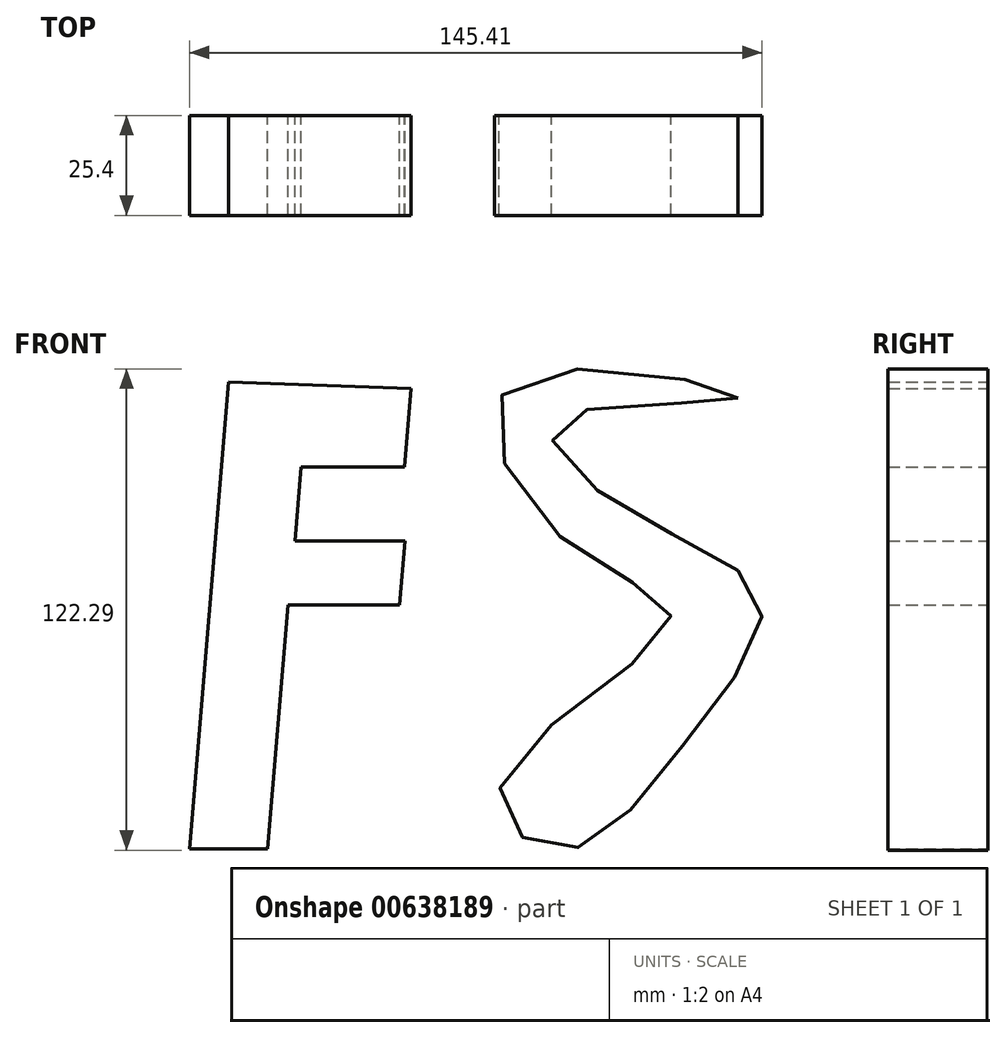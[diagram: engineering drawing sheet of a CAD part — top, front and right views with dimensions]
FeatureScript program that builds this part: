
annotation { "Feature Type Name" : "Feature", "Feature Type Description" : "" }
export const myFeature = defineFeature(function(context is Context, id is Id, definition is map)
    precondition{}
    {
        {
            var Q0;
            Q0=qCreatedBy(makeId("Front.planeOp"),FACE);
            var sketch = newSketch(context, id + "F0", { "sketchPlane" : qUnion([Q0])});
            skLineSegment(sketch, "E0", {"start": v(-62.23, 64.34) * mm, "end": v(-72.13, -54.26) * mm});
            skLineSegment(sketch, "E1", {"start": v(-72.13, -54.26) * mm, "end": v(-52.33, -54.26) * mm});
            skLineSegment(sketch, "E2", {"start": v(-52.33, -54.26) * mm, "end": v(-47.17, 7.65) * mm});
            skLineSegment(sketch, "E3", {"start": v(-47.17, 7.65) * mm, "end": v(-18.79, 7.65) * mm});
            skLineSegment(sketch, "E4", {"start": v(-18.79, 7.65) * mm, "end": v(-17.43, 23.91) * mm});
            skLineSegment(sketch, "E5", {"start": v(-17.43, 23.91) * mm, "end": v(-45.37, 23.91) * mm});
            skLineSegment(sketch, "E6", {"start": v(-45.37, 23.91) * mm, "end": v(-43.8, 42.7) * mm});
            skLineSegment(sketch, "E7", {"start": v(-43.8, 42.7) * mm, "end": v(-17.5, 42.7) * mm});
            skLineSegment(sketch, "E8", {"start": v(-17.5, 42.7) * mm, "end": v(-15.84, 62.66) * mm});
            skLineSegment(sketch, "E9", {"start": v(-15.84, 62.66) * mm, "end": v(-62.23, 64.34) * mm});
            skFitSpline(sketch, "E10", {"points": [v(67.18, 60.3) * mm, v(10.54, 64.15) * mm, v(23.19, 24.01) * mm, v(49.95, 3.12) * mm, v(6.87, -38.3) * mm, v(21.9, -54.62) * mm, v(52.52, -28.96) * mm, v(72.86, 8.98) * mm, v(36.75, 33.18) * mm, v(21.9, 54.8) * mm, v(67.18, 60.3) * mm]});
            skSolve(sketch);
        }
        {
            var Q0;
            Q0=makeQuery(id+"F0.imprint","IMPRINT",FACE,{"disambiguationData":[TD([[makeQuery(id+"F0.imprint","IMPRINT",EDGE,{"derivedFrom":sQuery(id+"F0.wireOp",EDGE,"E10")}),1.0]])]});
            var Q1;
            Q1=makeQuery(id+"F0.imprint","IMPRINT",FACE,{"disambiguationData":[TD([[makeQuery(id+"F0.imprint","IMPRINT",EDGE,{"derivedFrom":sQuery(id+"F0.wireOp",EDGE,"E0")}),1.0]])]});
            extrude(context, id + "F1", {"entities" : qUnion([Q0, Q1]), "depth" : 25.4 * mm, "offsetDistance" : 25.4 * mm});
        }
    });
